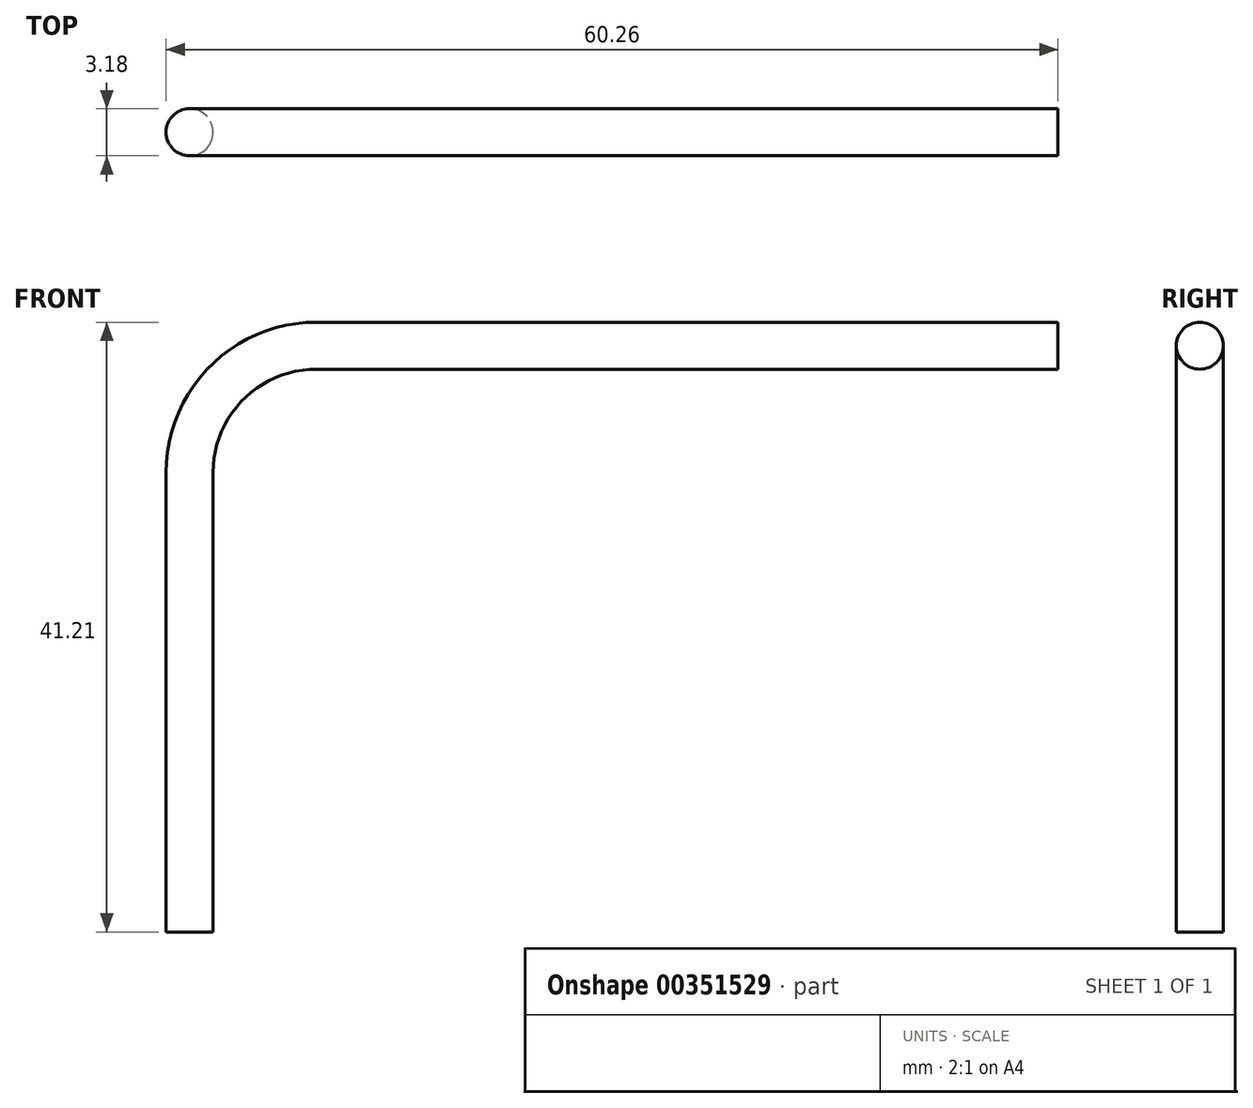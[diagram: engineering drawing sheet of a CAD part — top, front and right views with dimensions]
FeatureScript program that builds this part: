
annotation { "Feature Type Name" : "Feature", "Feature Type Description" : "" }
export const myFeature = defineFeature(function(context is Context, id is Id, definition is map)
    precondition{}
    {
        {
            var Q0;
            Q0=qCreatedBy(makeId("Front.planeOp"),FACE);
            var sketch = newSketch(context, id + "F0", { "sketchPlane" : qUnion([Q0])});
            skLineSegment(sketch, "E0", {"start": v(-38.28, 27.97) * mm, "end": v(23.01, 27.97) * mm, "construction": true});
            skLineSegment(sketch, "E1", {"start": v(-37.38, -11.65) * mm, "end": v(22.96, -11.65) * mm, "construction": true});
            skLineSegment(sketch, "E2", {"start": v(-22.88, -11.65) * mm, "end": v(-22.88, 19.4) * mm});
            skArc(sketch, "E3", {"start": v(-14.32, 27.97) * mm, "mid": v(-20.37, 25.47) * mm, "end": v(-22.88, 19.4) * mm});
            skLineSegment(sketch, "E4", {"start": v(-14.32, 27.97) * mm, "end": v(35.8, 27.97) * mm});
            skLineSegment(sketch, "E5", {"start": v(35.8, 27.97) * mm, "end": v(35.8, -11.65) * mm, "construction": true});
            skLineSegment(sketch, "E6", {"start": v(-22.88, 27.97) * mm, "end": v(-22.88, -11.65) * mm, "construction": true});
            skSolve(sketch);
        }
        {
            var Q0;
            Q0=qCreatedBy(makeId("Right.planeOp"),FACE);
            var Q1;
            Q1=sQuery(id+"F0.wireOp",VERTEX,"E5.start");
            cPlane(context, id + "F1", {"entities" : qUnion([Q0, Q1]), "cplaneType" : CPlaneType.PLANE_POINT, "offset" : 25.4 * mm, "width" : 152.4 * mm, "height" : 152.4 * mm});
        }
        {
            var Q0;
            Q0=qCreatedBy(id+"F1.planeOp",FACE);
            var sketch = newSketch(context, id + "F2", { "sketchPlane" : qUnion([Q0])});
            skCircle(sketch, "E7", {"center": v(0, 27.97) * mm, "radius": 1.59 * mm});
            skSolve(sketch);
        }
        {
            var Q0;
            Q0 = qSketchRegion(id + "F2", true);
            var Q1;
            Q1 = qConstructionFilter(qBodyType(qCreatedBy(id + "F0" ,EDGE), BodyType.WIRE), ConstructionObject.NO);
            sweep(context, id + "F3", {"profiles" : qUnion([Q0]), "path" : qUnion([Q1])});
        }
    });
